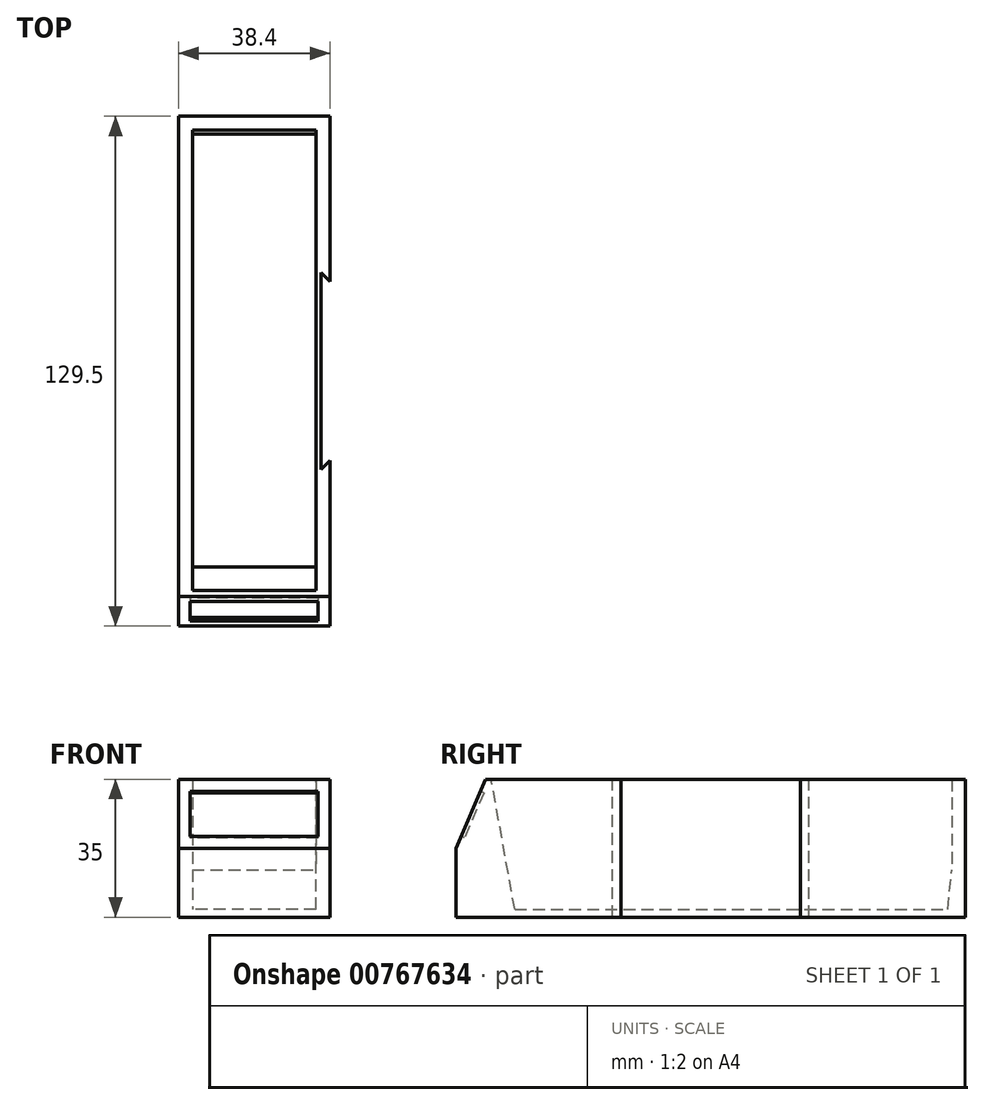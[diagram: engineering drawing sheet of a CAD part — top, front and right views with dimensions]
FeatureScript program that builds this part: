
annotation { "Feature Type Name" : "Feature", "Feature Type Description" : "" }
export const myFeature = defineFeature(function(context is Context, id is Id, definition is map)
    precondition{}
    {
        {
            var Q0;
            Q0=qCreatedBy(makeId("Top.planeOp"),FACE);
            var sketch = newSketch(context, id + "F0", { "sketchPlane" : qUnion([Q0])});
            skLineSegment(sketch, "E0.bottom", {"start": v(15.7, 55.5) * mm, "end": v(-15.7, 55.5) * mm});
            skLineSegment(sketch, "E0.top", {"start": v(15.7, -55.5) * mm, "end": v(-15.7, -55.5) * mm});
            skLineSegment(sketch, "E0.left", {"start": v(15.7, 55.5) * mm, "end": v(15.7, -55.5) * mm});
            skLineSegment(sketch, "E0.right", {"start": v(-15.7, 55.5) * mm, "end": v(-15.7, -55.5) * mm});
            skPoint(sketch, "E0.middle", {"position": v(0, 0) * mm});
            skLineSegment(sketch, "E1.bottom", {"start": v(19.2, -70.5) * mm, "end": v(-19.2, -70.5) * mm});
            skLineSegment(sketch, "E1.top", {"start": v(19.2, 59) * mm, "end": v(-19.2, 59) * mm});
            skLineSegment(sketch, "E1.left", {"start": v(19.2, -70.5) * mm, "end": v(19.2, 59) * mm});
            skLineSegment(sketch, "E1.right", {"start": v(-19.2, -70.5) * mm, "end": v(-19.2, 59) * mm});
            skPoint(sketch, "E1.middle", {"position": v(0, -5.75) * mm});
            skSolve(sketch);
        }
        {
            var Q0;
            Q0=qSketchRegion(id+"F0",true);
            var Q1;
            Q1=makeQuery(id+"F0.imprint","IMPRINT",FACE,{"disambiguationData":[TD([[makeQuery(id+"F0.imprint","IMPRINT",EDGE,{"derivedFrom":sQuery(id+"F0.wireOp",EDGE,"E0.bottom")}),1.0]])]});
            extrude(context, id + "F1", {"entities" : qUnion([Q0, Q1]), "depth" : 2 * mm, "offsetDistance" : 25 * mm});
        }
        {
            var Q0;
            Q0=makeQuery(id+"F0.imprint","IMPRINT",FACE,{"disambiguationData":[TD([[makeQuery(id+"F0.imprint","IMPRINT",EDGE,{"derivedFrom":sQuery(id+"F0.wireOp",EDGE,"E0.bottom")}),-1.0]])]});
            extrude(context, id + "F2", {"entities" : qUnion([Q0]), "operationType" : NewBodyOperationType.ADD, "depth" : 35 * mm, "offsetDistance" : 25 * mm});
        }
        {
            var Q0;
            Q0=makeQuery(id+"F2.opExtrude","CAP_EDGE",EDGE,{"disambiguationData":[OSD([sQuery(id+"F0.wireOp",EDGE,"E1.bottom")])],"isStart":false});
            chamfer(context, id + "F3", {"entities" : qUnion([Q0]), "chamferType" : ChamferType.TWO_OFFSETS, "width1" : 7.5 * mm, "oppositeDirection" : true, "width2" : 17.5 * mm, "tangentPropagation" : true});
        }
        {
            var Q0;
            Q0=makeQuery(id+"F2.opExtrude","CAP_EDGE",EDGE,{"disambiguationData":[OSD([sQuery(id+"F0.wireOp",EDGE,"E0.top")])],"isStart":false});
            chamfer(context, id + "F4", {"entities" : qUnion([Q0]), "chamferType" : ChamferType.TWO_OFFSETS, "width1" : 6 * mm, "oppositeDirection" : false, "width2" : 33 * mm, "tangentPropagation" : true});
        }
        {
            var Q0;
            Q0=makeQuery(id+"F2.opExtrude","CAP_FACE",FACE,{"disambiguationData":[OSD([sQuery(id+"F0.wireOp",EDGE,"E0.bottom"),sQuery(id+"F0.wireOp",EDGE,"E0.top"),sQuery(id+"F0.wireOp",EDGE,"E0.left"),sQuery(id+"F0.wireOp",EDGE,"E0.right"),sQuery(id+"F0.wireOp",EDGE,"E1.bottom"),sQuery(id+"F0.wireOp",EDGE,"E1.top"),sQuery(id+"F0.wireOp",EDGE,"E1.left"),sQuery(id+"F0.wireOp",EDGE,"E1.right")])],"isStart":false});
            var sketch = newSketch(context, id + "F5", { "sketchPlane" : qUnion([Q0])});
            skLineSegment(sketch, "E2", {"start": v(19.2, 17) * mm, "end": v(16.95, 19.25) * mm});
            skLineSegment(sketch, "E3", {"start": v(16.95, 19.25) * mm, "end": v(16.95, -30.75) * mm});
            skLineSegment(sketch, "E4", {"start": v(16.95, -30.75) * mm, "end": v(19.2, -28.5) * mm});
            skPoint(sketch, "E5", {"position": v(16.95, -5.75) * mm});
            skLineSegment(sketch, "E6", {"start": v(19.2, 17) * mm, "end": v(19.2, -28.5) * mm});
            skLineSegment(sketch, "E7", {"start": v(-19.2, 19.25) * mm, "end": v(-16.95, 17) * mm, "construction": true});
            skLineSegment(sketch, "E8", {"start": v(-19.2, -30.75) * mm, "end": v(-16.95, -28.5) * mm, "construction": true});
            skLineSegment(sketch, "E9", {"start": v(-16.95, -28.5) * mm, "end": v(-16.95, 17) * mm, "construction": true});
            skLineSegment(sketch, "E10", {"start": v(-16.95, 17) * mm, "end": v(-16.95, 59) * mm});
            skLineSegment(sketch, "E11", {"start": v(-16.95, 59) * mm, "end": v(-19.2, 59) * mm});
            skLineSegment(sketch, "E12", {"start": v(-19.2, 59) * mm, "end": v(-19.2, 19.25) * mm});
            skLineSegment(sketch, "E13", {"start": v(-16.95, -28.5) * mm, "end": v(-16.95, -70.5) * mm});
            skLineSegment(sketch, "E14", {"start": v(-16.95, -70.5) * mm, "end": v(-19.2, -70.5) * mm});
            skLineSegment(sketch, "E15", {"start": v(-19.2, -70.5) * mm, "end": v(-19.2, -30.75) * mm});
            skLineSegment(sketch, "E16", {"start": v(-19.2, 19.4) * mm, "end": v(-16.95, 17.14) * mm});
            skLineSegment(sketch, "E17", {"start": v(-19.2, -30.9) * mm, "end": v(-16.95, -28.64) * mm});
            skSolve(sketch);
        }
        {
            var Q0;
            Q0=makeQuery(id+"F5.imprint","IMPRINT",FACE,{"disambiguationData":[TD([[makeQuery(id+"F5.imprint","IMPRINT",EDGE,{"derivedFrom":sQuery(id+"F5.wireOp",EDGE,"E2")}),1.0]])]});
            extrude(context, id + "F6", {"entities" : qUnion([Q0]), "operationType" : NewBodyOperationType.REMOVE, "endBound" : BoundingType.THROUGH_ALL, "oppositeDirection" : true, "depth" : 25 * mm, "offsetDistance" : 25 * mm});
        }
        {
            var Q0;
            Q0=makeQuery(id+"F3.opChamfer","BLEND_FACE",FACE,{"disambiguationData":[OSD([sQuery(id+"F0.wireOp",EDGE,"E1.bottom")])]});
            var sketch = newSketch(context, id + "F7", { "sketchPlane" : qUnion([Q0])});
            skLineSegment(sketch, "E18.bottom", {"start": v(16.25, 4.08) * mm, "end": v(-16.25, 4.08) * mm});
            skLineSegment(sketch, "E18.top", {"start": v(16.25, -8.42) * mm, "end": v(-16.25, -8.42) * mm});
            skLineSegment(sketch, "E18.left", {"start": v(16.25, 4.08) * mm, "end": v(16.25, -8.42) * mm});
            skLineSegment(sketch, "E18.right", {"start": v(-16.25, 4.08) * mm, "end": v(-16.25, -8.42) * mm});
            skPoint(sketch, "E18.middle", {"position": v(0, -2.17) * mm});
            skPoint(sketch, "E18.middle.positionSnap0", {"position": v(0, 7.35) * mm});
            skPoint(sketch, "E18.centerSnap0", {"position": v(0, 7.35) * mm});
            skSolve(sketch);
        }
        {
            var Q0;
            Q0=qSketchRegion(id+"F7",true);
            extrude(context, id + "F8", {"entities" : qUnion([Q0]), "operationType" : NewBodyOperationType.REMOVE, "oppositeDirection" : true, "depth" : 1 * mm, "offsetDistance" : 25 * mm});
        }
        {
            var Q0;
            Q0=makeQuery(id+"F2.boolean.opBoolean","INTERSECT",EDGE,{"derivedFrom":[makeQuery(id+"F1.opExtrude","CAP_FACE",FACE,{"disambiguationData":[OSD([sQuery(id+"F0.wireOp",EDGE,"E1.bottom"),sQuery(id+"F0.wireOp",EDGE,"E1.top"),sQuery(id+"F0.wireOp",EDGE,"E1.left"),sQuery(id+"F0.wireOp",EDGE,"E1.right")])],"isStart":false}),makeQuery(id+"F2.opExtrude","SWEPT_FACE",FACE,{"disambiguationData":[OSD([sQuery(id+"F0.wireOp",EDGE,"E0.bottom")])]})]});
            chamfer(context, id + "F9", {"entities" : qUnion([Q0]), "chamferType" : ChamferType.TWO_OFFSETS, "width1" : 1 * mm, "oppositeDirection" : true, "width2" : 10 * mm, "tangentPropagation" : true});
        }
    });
